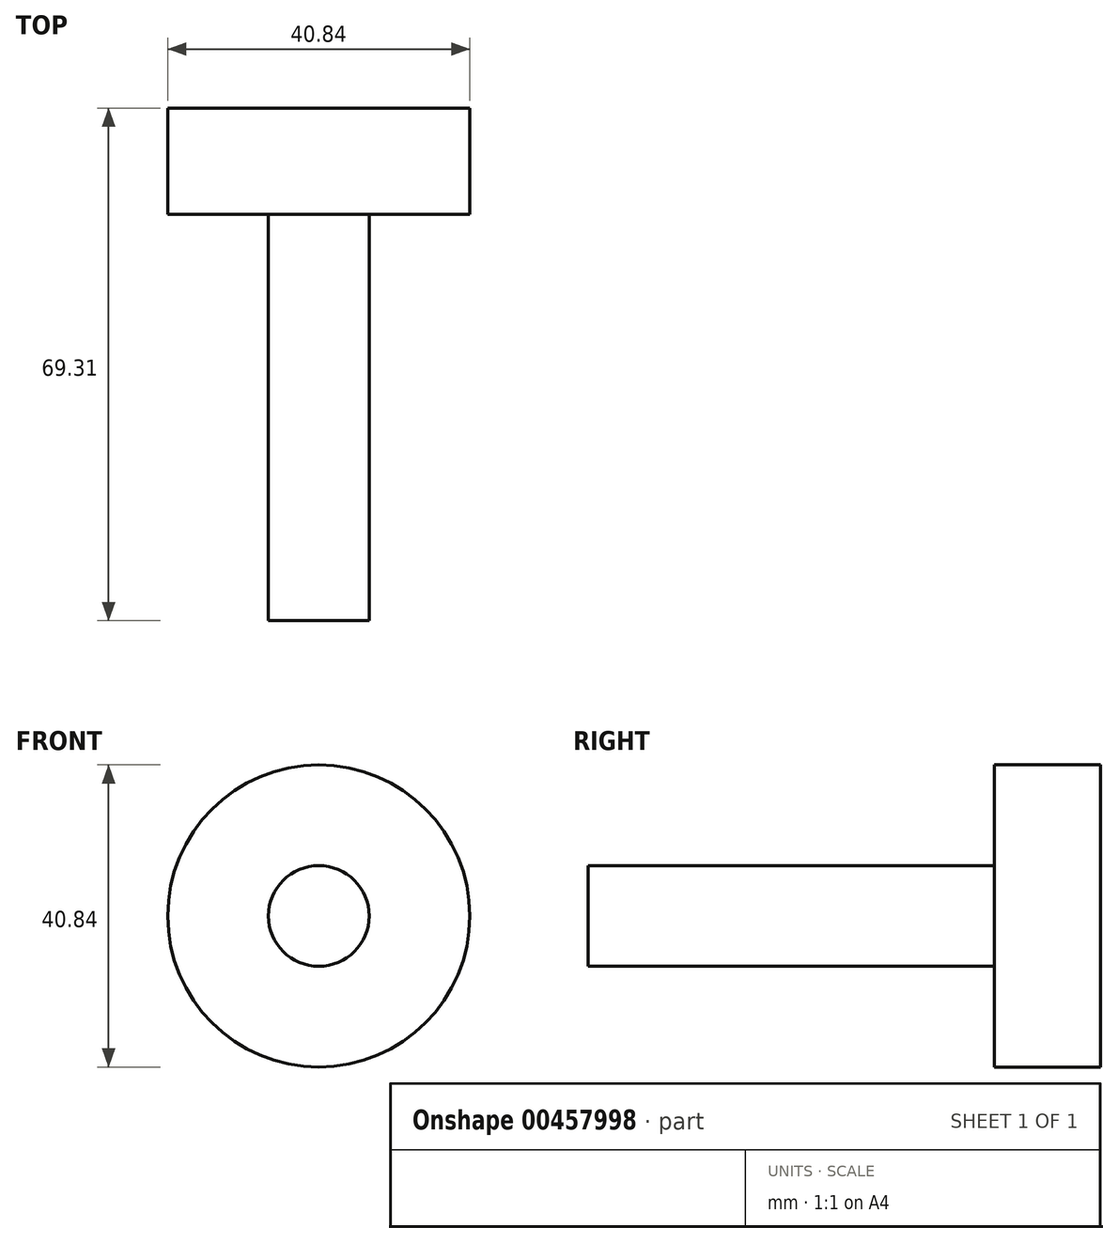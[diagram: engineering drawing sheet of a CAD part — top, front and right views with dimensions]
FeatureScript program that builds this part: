
annotation { "Feature Type Name" : "Feature", "Feature Type Description" : "" }
export const myFeature = defineFeature(function(context is Context, id is Id, definition is map)
    precondition{}
    {
        {
            var Q0;
            Q0=qCreatedBy(makeId("Top.planeOp"),FACE);
            var sketch = newSketch(context, id + "F0", { "sketchPlane" : qUnion([Q0])});
            skLineSegment(sketch, "E0", {"start": v(0, 14.39) * mm, "end": v(20.42, 14.39) * mm});
            skLineSegment(sketch, "E1", {"start": v(20.42, 14.39) * mm, "end": v(20.42, 0) * mm});
            skLineSegment(sketch, "E2", {"start": v(20.42, 0) * mm, "end": v(6.8, 0) * mm});
            skLineSegment(sketch, "E3", {"start": v(6.8, 0) * mm, "end": v(6.8, -54.92) * mm});
            skLineSegment(sketch, "E4", {"start": v(6.8, -54.92) * mm, "end": v(0, -54.92) * mm});
            skLineSegment(sketch, "E5", {"start": v(0, -54.92) * mm, "end": v(0, 14.39) * mm});
            skSolve(sketch);
        }
        {
            var Q0;
            Q0 = qSketchRegion(id + "F0", true);
            var Q1;
            Q1=sQuery(id+"F0.wireOp",EDGE,"E5");
            revolve(context, id + "F1", {"entities" : qUnion([Q0]), "axis" : qUnion([Q1]), "revolveType" : RevolveType.FULL});
        }
        {
            var Q0;
            Q0=qCreatedBy(makeId("Front.planeOp"),FACE);
            var sketch = newSketch(context, id + "F2", { "sketchPlane" : qUnion([Q0])});
            skCircle(sketch, "E6.cCircle", {"center": v(0, 0) * mm, "radius": 4.83 * mm, "construction": true});
            skLineSegment(sketch, "E6.0", {"start": v(2.93, 4.75) * mm, "end": v(5.58, -0.16) * mm});
            skLineSegment(sketch, "E6.1", {"start": v(5.58, -0.16) * mm, "end": v(2.65, -4.91) * mm});
            skLineSegment(sketch, "E6.2", {"start": v(2.65, -4.91) * mm, "end": v(-2.93, -4.75) * mm});
            skLineSegment(sketch, "E6.3", {"start": v(-2.93, -4.75) * mm, "end": v(-5.58, 0.16) * mm});
            skLineSegment(sketch, "E6.4", {"start": v(-5.58, 0.16) * mm, "end": v(-2.65, 4.91) * mm});
            skLineSegment(sketch, "E6.5", {"start": v(-2.65, 4.91) * mm, "end": v(2.93, 4.75) * mm});
            skPoint(sketch, "E6.0.midPoint", {"position": v(4.25, 2.3) * mm});
            skSolve(sketch);
        }
        {
            var Q0;
            Q0 = qSketchRegion(id + "F2", true);
            var Q1;
            Q1=makeQuery(id+"F1.opRevolve","SWEPT_FACE",FACE,{"disambiguationData":[OSD([sQuery(id+"F0.wireOp",EDGE,"E0")])]});
            extrude(context, id + "F3", {"entities" : qUnion([Q0, Q1]), "operationType" : NewBodyOperationType.ADD, "depth" : 10 * mm});
        }
    });
